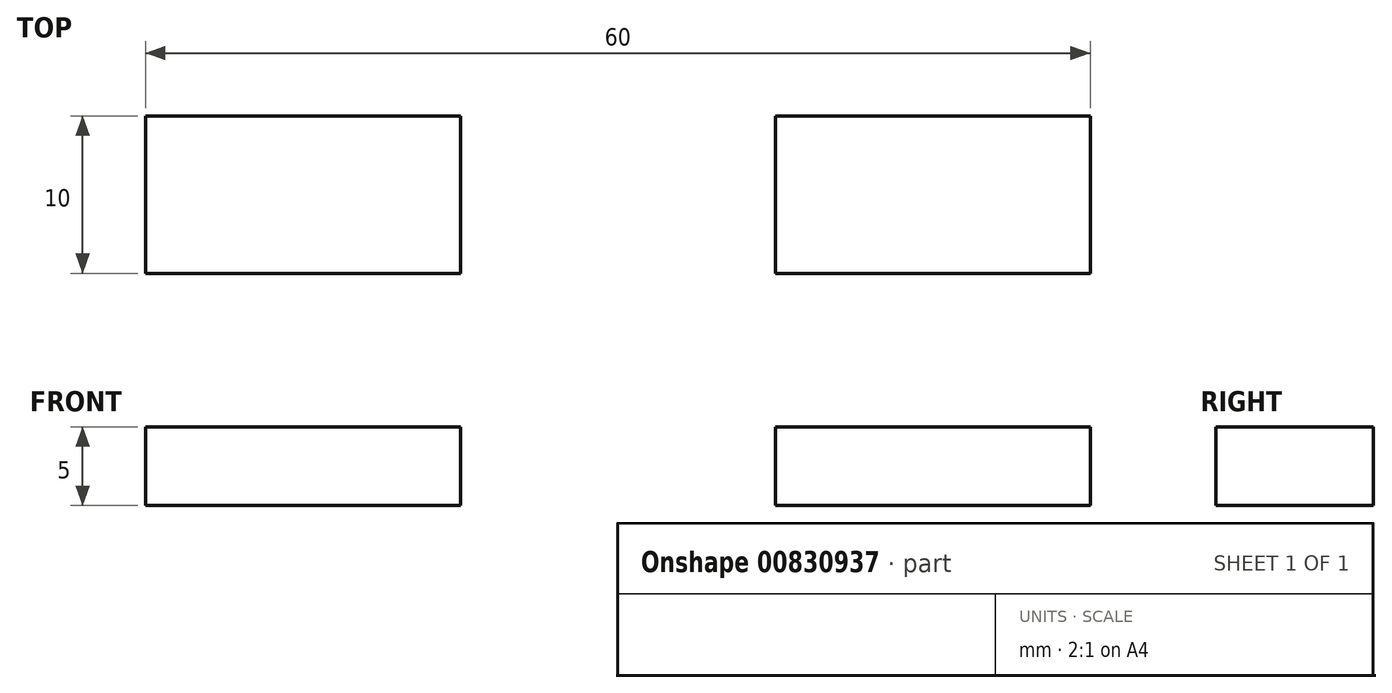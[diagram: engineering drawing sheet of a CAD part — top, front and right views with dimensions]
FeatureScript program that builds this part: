
annotation { "Feature Type Name" : "Feature", "Feature Type Description" : "" }
export const myFeature = defineFeature(function(context is Context, id is Id, definition is map)
    precondition{}
    {
        {
            var Q0;
            Q0=qCreatedBy(makeId("Top.planeOp"),FACE);
            var sketch = newSketch(context, id + "F0", { "sketchPlane" : qUnion([Q0])});
            skLineSegment(sketch, "E0.bottom", {"start": v(43.1, -38.2) * mm, "end": v(63.1, -38.2) * mm});
            skLineSegment(sketch, "E0.top", {"start": v(43.1, -48.2) * mm, "end": v(63.1, -48.2) * mm});
            skLineSegment(sketch, "E0.left", {"start": v(43.1, -38.2) * mm, "end": v(43.1, -48.2) * mm});
            skLineSegment(sketch, "E0.right", {"start": v(63.1, -38.2) * mm, "end": v(63.1, -48.2) * mm});
            skSolve(sketch);
        }
        {
            var Q0;
            Q0=makeQuery(id+"F0.imprint","IMPRINT",FACE,{"disambiguationData":[TD([[makeQuery(id+"F0.imprint","IMPRINT",EDGE,{"derivedFrom":sQuery(id+"F0.wireOp",EDGE,"E0.bottom")}),-1.0]])]});
            extrude(context, id + "F1", {"entities" : qUnion([Q0]), "depth" : 5 * mm, "offsetDistance" : 25 * mm});
        }
        {
            var Q0;
            Q0=qCreatedBy(makeId("Top.planeOp"),FACE);
            var sketch = newSketch(context, id + "F2", { "sketchPlane" : qUnion([Q0])});
            skLineSegment(sketch, "E1.bottom", {"start": v(83.1, -38.2) * mm, "end": v(103.1, -38.2) * mm});
            skLineSegment(sketch, "E1.top", {"start": v(83.1, -48.2) * mm, "end": v(103.1, -48.2) * mm});
            skLineSegment(sketch, "E1.left", {"start": v(83.1, -38.2) * mm, "end": v(83.1, -48.2) * mm});
            skLineSegment(sketch, "E1.right", {"start": v(103.1, -38.2) * mm, "end": v(103.1, -48.2) * mm});
            skLineSegment(sketch, "E2", {"start": v(44.27, -88.2) * mm, "end": v(122.13, -88.2) * mm});
            skSolve(sketch);
        }
        {
            var Q0;
            Q0=makeQuery(id+"F2.imprint","IMPRINT",FACE,{"disambiguationData":[TD([[makeQuery(id+"F2.imprint","IMPRINT",EDGE,{"derivedFrom":sQuery(id+"F2.wireOp",EDGE,"E1.bottom")}),-1.0]])]});
            extrude(context, id + "F3", {"entities" : qUnion([Q0]), "depth" : 5 * mm, "offsetDistance" : 25 * mm});
        }
    });
